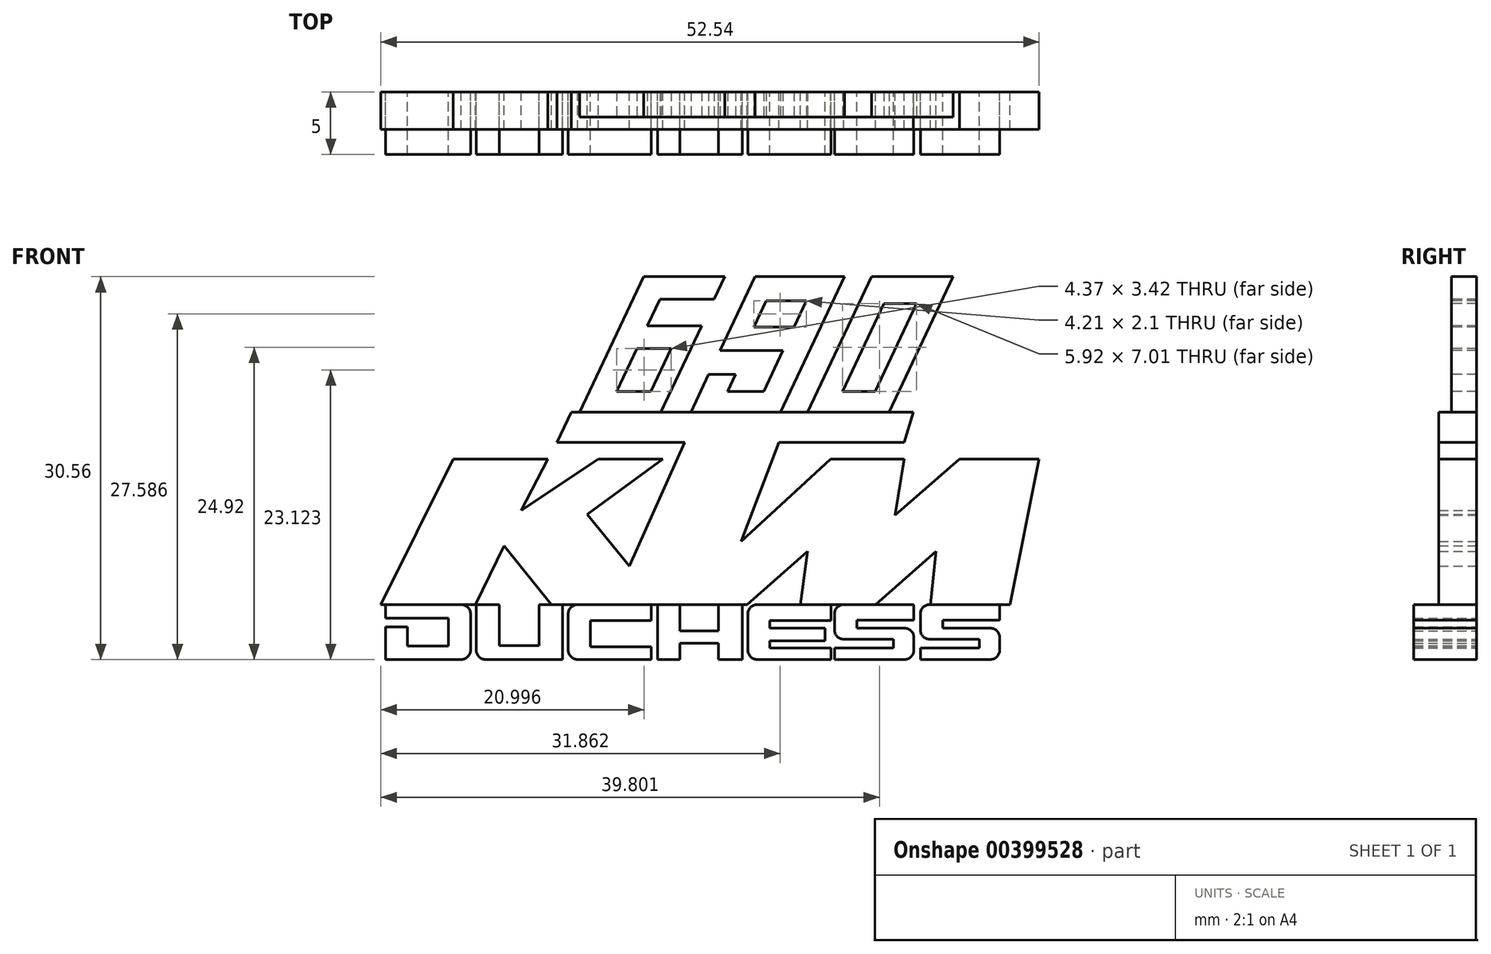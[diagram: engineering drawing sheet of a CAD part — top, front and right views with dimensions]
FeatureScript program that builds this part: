
annotation { "Feature Type Name" : "Feature", "Feature Type Description" : "" }
export const myFeature = defineFeature(function(context is Context, id is Id, definition is map)
    precondition{}
    {
        {
            var Q0;
            Q0=qCreatedBy(makeId("Front.planeOp"),FACE);
            var sketch = newSketch(context, id + "F0", { "sketchPlane" : qUnion([Q0])});
            skLineSegment(sketch, "E0", {"start": v(-21, 3.08) * mm, "end": v(-26.77, -8.53) * mm});
            skLineSegment(sketch, "E1", {"start": v(-19.24, -8.53) * mm, "end": v(-16.95, -3.85) * mm});
            skLineSegment(sketch, "E2", {"start": v(-16.95, -3.85) * mm, "end": v(-13.14, -8.53) * mm});
            skLineSegment(sketch, "E3", {"start": v(2.46, -8.53) * mm, "end": v(7.3, -4.3) * mm});
            skLineSegment(sketch, "E4", {"start": v(7.3, -4.3) * mm, "end": v(6.73, -8.53) * mm});
            skLineSegment(sketch, "E5", {"start": v(12.72, -8.53) * mm, "end": v(17.55, -4.3) * mm});
            skLineSegment(sketch, "E6", {"start": v(17.55, -4.3) * mm, "end": v(17.09, -8.53) * mm});
            skLineSegment(sketch, "E7", {"start": v(22.64, -8.53) * mm, "end": v(23.45, -8.53) * mm});
            skLineSegment(sketch, "E8", {"start": v(23.45, -8.53) * mm, "end": v(25.77, 3.08) * mm});
            skLineSegment(sketch, "E9", {"start": v(25.77, 3.08) * mm, "end": v(19.43, 3.08) * mm});
            skLineSegment(sketch, "E10", {"start": v(19.43, 3.08) * mm, "end": v(14.26, -1.4) * mm});
            skLineSegment(sketch, "E11", {"start": v(14.26, -1.4) * mm, "end": v(15.01, 3.08) * mm});
            skLineSegment(sketch, "E12", {"start": v(15.01, 3.08) * mm, "end": v(9.11, 3.08) * mm});
            skLineSegment(sketch, "E13", {"start": v(9.11, 3.08) * mm, "end": v(1.98, -3.5) * mm});
            skLineSegment(sketch, "E14", {"start": v(1.98, -3.5) * mm, "end": v(5, 4.43) * mm});
            skLineSegment(sketch, "E15", {"start": v(5, 4.43) * mm, "end": v(15.01, 4.43) * mm});
            skLineSegment(sketch, "E16", {"start": v(15.01, 4.43) * mm, "end": v(15.73, 6.81) * mm});
            skLineSegment(sketch, "E17", {"start": v(-11.58, 6.81) * mm, "end": v(-12.71, 4.43) * mm});
            skLineSegment(sketch, "E18", {"start": v(-12.71, 4.43) * mm, "end": v(-2.53, 4.43) * mm});
            skLineSegment(sketch, "E19", {"start": v(-2.53, 4.43) * mm, "end": v(-6.92, -5.47) * mm});
            skLineSegment(sketch, "E20", {"start": v(-6.92, -5.47) * mm, "end": v(-10.29, -1.32) * mm});
            skLineSegment(sketch, "E21", {"start": v(-10.29, -1.32) * mm, "end": v(-4.27, 3.08) * mm});
            skLineSegment(sketch, "E22", {"start": v(-4.27, 3.08) * mm, "end": v(-9.42, 3.08) * mm});
            skLineSegment(sketch, "E23", {"start": v(-9.42, 3.08) * mm, "end": v(-15.58, -1.03) * mm});
            skLineSegment(sketch, "E24", {"start": v(-15.58, -1.03) * mm, "end": v(-13.45, 3.08) * mm});
            skLineSegment(sketch, "E25", {"start": v(-13.45, 3.08) * mm, "end": v(-21, 3.08) * mm});
            skLineSegment(sketch, "E26", {"start": v(-26.4, -8.53) * mm, "end": v(-26.4, -9.64) * mm});
            skLineSegment(sketch, "E27", {"start": v(-26.4, -12.92) * mm, "end": v(-20.36, -12.92) * mm});
            skLineSegment(sketch, "E28", {"start": v(-19.6, -12.17) * mm, "end": v(-19.6, -9.28) * mm});
            skPoint(sketch, "E29.visualSharp", {"position": v(-19.6, -8.53) * mm});
            skArc(sketch, "E29.filletArc", {"start": v(-19.6, -9.28) * mm, "mid": v(-19.83, -8.75) * mm, "end": v(-20.36, -8.53) * mm});
            skPoint(sketch, "E30.visualSharp", {"position": v(-19.6, -12.92) * mm});
            skArc(sketch, "E30.filletArc", {"start": v(-20.36, -12.92) * mm, "mid": v(-19.83, -12.7) * mm, "end": v(-19.6, -12.17) * mm});
            skLineSegment(sketch, "E31", {"start": v(-24.66, -10.31) * mm, "end": v(-24.66, -11.84) * mm});
            skLineSegment(sketch, "E32", {"start": v(-24.66, -11.84) * mm, "end": v(-21.39, -11.84) * mm});
            skLineSegment(sketch, "E33", {"start": v(-21.39, -11.84) * mm, "end": v(-21.39, -9.64) * mm});
            skLineSegment(sketch, "E34", {"start": v(-21.39, -9.64) * mm, "end": v(-26.4, -9.64) * mm});
            skLineSegment(sketch, "E35", {"start": v(-24.66, -10.31) * mm, "end": v(-26.4, -10.31) * mm});
            skLineSegment(sketch, "E36.trimOffspring", {"start": v(-26.4, -10.31) * mm, "end": v(-26.4, -12.92) * mm});
            skLineSegment(sketch, "E37", {"start": v(-20.36, -8.53) * mm, "end": v(-19.17, -8.53) * mm, "construction": true});
            skLineSegment(sketch, "E38", {"start": v(-19.17, -8.53) * mm, "end": v(-19.17, -12.17) * mm});
            skLineSegment(sketch, "E39", {"start": v(-17.3, -8.53) * mm, "end": v(-17.3, -11.81) * mm});
            skLineSegment(sketch, "E40", {"start": v(-17.3, -11.81) * mm, "end": v(-14.13, -11.81) * mm});
            skLineSegment(sketch, "E41", {"start": v(-14.13, -11.81) * mm, "end": v(-14.13, -8.53) * mm});
            skLineSegment(sketch, "E42", {"start": v(-14.13, -8.53) * mm, "end": v(-13.14, -8.53) * mm});
            skLineSegment(sketch, "E43", {"start": v(-12.28, -8.53) * mm, "end": v(-12.28, -12.92) * mm});
            skLineSegment(sketch, "E44", {"start": v(-12.28, -12.92) * mm, "end": v(-18.42, -12.92) * mm});
            skPoint(sketch, "E45.visualSharp", {"position": v(-19.17, -12.92) * mm});
            skArc(sketch, "E45.filletArc", {"start": v(-19.17, -12.17) * mm, "mid": v(-18.95, -12.7) * mm, "end": v(-18.42, -12.92) * mm});
            skLineSegment(sketch, "E46", {"start": v(-19.17, -8.53) * mm, "end": v(-17.3, -8.53) * mm});
            skLineSegment(sketch, "E47", {"start": v(-11.82, -9.28) * mm, "end": v(-11.82, -12.17) * mm});
            skLineSegment(sketch, "E48", {"start": v(-5.18, -8.53) * mm, "end": v(-5.18, -9.8) * mm});
            skLineSegment(sketch, "E49", {"start": v(-5.18, -9.8) * mm, "end": v(-10.05, -9.8) * mm});
            skLineSegment(sketch, "E50", {"start": v(-10.05, -9.8) * mm, "end": v(-10.05, -11.91) * mm});
            skLineSegment(sketch, "E51", {"start": v(-10.05, -11.91) * mm, "end": v(-5.18, -11.91) * mm});
            skLineSegment(sketch, "E52", {"start": v(-5.18, -11.91) * mm, "end": v(-5.18, -12.92) * mm});
            skLineSegment(sketch, "E53", {"start": v(-11.07, -12.92) * mm, "end": v(-5.18, -12.92) * mm});
            skPoint(sketch, "E54.visualSharp", {"position": v(-11.82, -12.92) * mm});
            skArc(sketch, "E54.filletArc", {"start": v(-11.82, -12.17) * mm, "mid": v(-11.6, -12.7) * mm, "end": v(-11.07, -12.92) * mm});
            skPoint(sketch, "E55.visualSharp", {"position": v(-11.82, -8.53) * mm});
            skArc(sketch, "E55.filletArc", {"start": v(-11.07, -8.53) * mm, "mid": v(-11.6, -8.75) * mm, "end": v(-11.82, -9.28) * mm});
            skLineSegment(sketch, "E56", {"start": v(-4.69, -8.53) * mm, "end": v(-4.69, -12.92) * mm});
            skLineSegment(sketch, "E57", {"start": v(-4.69, -12.92) * mm, "end": v(-2.9, -12.92) * mm});
            skLineSegment(sketch, "E58", {"start": v(-2.9, -12.92) * mm, "end": v(-2.9, -11.62) * mm});
            skLineSegment(sketch, "E59", {"start": v(-2.9, -11.62) * mm, "end": v(0.17, -11.62) * mm});
            skLineSegment(sketch, "E60", {"start": v(0.17, -11.62) * mm, "end": v(0.17, -12.92) * mm});
            skLineSegment(sketch, "E61", {"start": v(0.17, -12.92) * mm, "end": v(2.1, -12.92) * mm});
            skLineSegment(sketch, "E62", {"start": v(2.1, -12.92) * mm, "end": v(2.1, -8.53) * mm});
            skLineSegment(sketch, "E63", {"start": v(0.17, -8.53) * mm, "end": v(0.17, -10.63) * mm});
            skLineSegment(sketch, "E64", {"start": v(0.17, -10.63) * mm, "end": v(-2.9, -10.63) * mm});
            skLineSegment(sketch, "E65", {"start": v(-2.9, -10.63) * mm, "end": v(-2.9, -8.53) * mm});
            skLineSegment(sketch, "E66", {"start": v(2.52, -9.28) * mm, "end": v(2.52, -12.17) * mm});
            skLineSegment(sketch, "E67", {"start": v(9.16, -8.53) * mm, "end": v(9.16, -9.8) * mm});
            skLineSegment(sketch, "E68", {"start": v(9.16, -9.8) * mm, "end": v(4.28, -9.8) * mm});
            skLineSegment(sketch, "E69", {"start": v(4.28, -9.8) * mm, "end": v(4.28, -10.41) * mm});
            skLineSegment(sketch, "E70", {"start": v(4.28, -12) * mm, "end": v(9.16, -12) * mm});
            skLineSegment(sketch, "E71", {"start": v(9.16, -12) * mm, "end": v(9.16, -12.92) * mm});
            skLineSegment(sketch, "E72", {"start": v(3.27, -12.92) * mm, "end": v(9.16, -12.92) * mm});
            skPoint(sketch, "E73.visualSharp", {"position": v(2.52, -12.92) * mm});
            skArc(sketch, "E73.filletArc", {"start": v(2.52, -12.17) * mm, "mid": v(2.74, -12.7) * mm, "end": v(3.27, -12.92) * mm});
            skLineSegment(sketch, "E74", {"start": v(3.27, -8.53) * mm, "end": v(6.73, -8.53) * mm});
            skPoint(sketch, "E75.visualSharp", {"position": v(2.52, -8.53) * mm});
            skArc(sketch, "E75.filletArc", {"start": v(3.27, -8.53) * mm, "mid": v(2.74, -8.75) * mm, "end": v(2.52, -9.28) * mm});
            skLineSegment(sketch, "E76", {"start": v(8.69, -10.41) * mm, "end": v(4.28, -10.41) * mm});
            skLineSegment(sketch, "E77", {"start": v(8.69, -10.41) * mm, "end": v(8.69, -11.45) * mm});
            skLineSegment(sketch, "E78", {"start": v(8.69, -11.45) * mm, "end": v(4.28, -11.45) * mm});
            skLineSegment(sketch, "E79.trimOffspring", {"start": v(4.28, -11.45) * mm, "end": v(4.28, -12) * mm});
            skLineSegment(sketch, "E80", {"start": v(15.78, -8.53) * mm, "end": v(15.78, -9.77) * mm});
            skLineSegment(sketch, "E81", {"start": v(15.78, -9.77) * mm, "end": v(11.21, -9.77) * mm});
            skLineSegment(sketch, "E82", {"start": v(11.21, -9.77) * mm, "end": v(11.21, -10.42) * mm});
            skLineSegment(sketch, "E83", {"start": v(11.21, -10.42) * mm, "end": v(15.03, -10.42) * mm});
            skLineSegment(sketch, "E84", {"start": v(15.78, -11.17) * mm, "end": v(15.78, -12.17) * mm});
            skLineSegment(sketch, "E85", {"start": v(15.03, -12.92) * mm, "end": v(9.43, -12.92) * mm});
            skLineSegment(sketch, "E86", {"start": v(9.43, -12.92) * mm, "end": v(9.43, -12) * mm});
            skLineSegment(sketch, "E87", {"start": v(9.43, -12) * mm, "end": v(14.16, -12) * mm});
            skLineSegment(sketch, "E88", {"start": v(14.16, -12) * mm, "end": v(14.16, -11.3) * mm});
            skLineSegment(sketch, "E89", {"start": v(14.16, -11.3) * mm, "end": v(10.18, -11.3) * mm});
            skLineSegment(sketch, "E90", {"start": v(9.43, -10.55) * mm, "end": v(9.43, -9.28) * mm});
            skLineSegment(sketch, "E91", {"start": v(12.72, -8.53) * mm, "end": v(15.78, -8.53) * mm});
            skPoint(sketch, "E92.visualSharp", {"position": v(9.43, -8.53) * mm});
            skArc(sketch, "E92.filletArc", {"start": v(10.18, -8.53) * mm, "mid": v(9.65, -8.75) * mm, "end": v(9.43, -9.28) * mm});
            skPoint(sketch, "E93.visualSharp", {"position": v(9.43, -11.3) * mm});
            skArc(sketch, "E93.filletArc", {"start": v(9.43, -10.55) * mm, "mid": v(9.65, -11.08) * mm, "end": v(10.18, -11.3) * mm});
            skPoint(sketch, "E94.visualSharp", {"position": v(15.78, -10.42) * mm});
            skArc(sketch, "E94.filletArc", {"start": v(15.78, -11.17) * mm, "mid": v(15.56, -10.64) * mm, "end": v(15.03, -10.42) * mm});
            skPoint(sketch, "E95.visualSharp", {"position": v(15.78, -12.92) * mm});
            skArc(sketch, "E95.filletArc", {"start": v(15.03, -12.92) * mm, "mid": v(15.56, -12.7) * mm, "end": v(15.78, -12.17) * mm});
            skLineSegment(sketch, "E96", {"start": v(22.64, -8.53) * mm, "end": v(22.64, -9.77) * mm});
            skLineSegment(sketch, "E97", {"start": v(22.64, -9.77) * mm, "end": v(18.07, -9.77) * mm});
            skLineSegment(sketch, "E98", {"start": v(18.07, -9.77) * mm, "end": v(18.07, -10.42) * mm});
            skLineSegment(sketch, "E99", {"start": v(18.07, -10.42) * mm, "end": v(21.89, -10.42) * mm});
            skLineSegment(sketch, "E100", {"start": v(22.64, -11.17) * mm, "end": v(22.64, -12.17) * mm});
            skLineSegment(sketch, "E101", {"start": v(21.89, -12.92) * mm, "end": v(16.29, -12.92) * mm});
            skLineSegment(sketch, "E102", {"start": v(16.29, -12.92) * mm, "end": v(16.29, -12) * mm});
            skLineSegment(sketch, "E103", {"start": v(16.29, -12) * mm, "end": v(21.02, -12) * mm});
            skLineSegment(sketch, "E104", {"start": v(21.02, -12) * mm, "end": v(21.02, -11.3) * mm});
            skLineSegment(sketch, "E105", {"start": v(21.02, -11.3) * mm, "end": v(17.04, -11.3) * mm});
            skLineSegment(sketch, "E106", {"start": v(16.29, -10.55) * mm, "end": v(16.29, -9.28) * mm});
            skLineSegment(sketch, "E107", {"start": v(17.04, -8.53) * mm, "end": v(17.09, -8.53) * mm});
            skPoint(sketch, "E108.visualSharp", {"position": v(16.29, -8.53) * mm});
            skArc(sketch, "E108.filletArc", {"start": v(17.04, -8.53) * mm, "mid": v(16.5, -8.75) * mm, "end": v(16.29, -9.28) * mm});
            skPoint(sketch, "E109.visualSharp", {"position": v(16.29, -11.3) * mm});
            skArc(sketch, "E109.filletArc", {"start": v(16.29, -10.55) * mm, "mid": v(16.5, -11.08) * mm, "end": v(17.04, -11.3) * mm});
            skPoint(sketch, "E110.visualSharp", {"position": v(22.64, -10.42) * mm});
            skArc(sketch, "E110.filletArc", {"start": v(22.64, -11.17) * mm, "mid": v(22.42, -10.64) * mm, "end": v(21.89, -10.42) * mm});
            skPoint(sketch, "E111.visualSharp", {"position": v(22.64, -12.92) * mm});
            skArc(sketch, "E111.filletArc", {"start": v(21.89, -12.92) * mm, "mid": v(22.42, -12.7) * mm, "end": v(22.64, -12.17) * mm});
            skLineSegment(sketch, "E112", {"start": v(23.45, -8.53) * mm, "end": v(22.64, -8.53) * mm});
            skPoint(sketch, "E113.orphan", {"position": v(-13.45, -8.15) * mm});
            skPoint(sketch, "E114.orphan", {"position": v(-19.05, -8.15) * mm});
            skLineSegment(sketch, "E115.trimOffspring", {"start": v(10.18, -8.53) * mm, "end": v(9.16, -8.53) * mm});
            skLineSegment(sketch, "E116.trimOffspring", {"start": v(2.46, -8.53) * mm, "end": v(2.1, -8.53) * mm});
            skLineSegment(sketch, "E117.trimOffspring", {"start": v(-19.24, -8.53) * mm, "end": v(-20.36, -8.53) * mm});
            skLineSegment(sketch, "E118.trimOffspring", {"start": v(-4.69, -8.53) * mm, "end": v(-5.18, -8.53) * mm});
            skLineSegment(sketch, "E119.trimOffspring", {"start": v(-11.07, -8.53) * mm, "end": v(-12.28, -8.53) * mm});
            skLineSegment(sketch, "E120.trimOffspring", {"start": v(-26.4, -8.53) * mm, "end": v(-26.77, -8.53) * mm});
            skLineSegment(sketch, "E121", {"start": v(-2.9, -8.53) * mm, "end": v(0.17, -8.53) * mm});
            skLineSegment(sketch, "E122", {"start": v(-11.58, 6.81) * mm, "end": v(15.73, 6.81) * mm});
            skSolve(sketch);
        }
        {
            var Q0;
            Q0=qSketchRegion(id+"F0",true);
            extrude(context, id + "F1", {"entities" : qUnion([Q0]), "depth" : 5 * mm});
        }
        {
            var Q0;
            Q0=makeQuery(id+"F1.opExtrude","CAP_FACE",FACE,{"disambiguationData":[OSD([sQuery(id+"F0.wireOp",EDGE,"E0"),sQuery(id+"F0.wireOp",EDGE,"E1"),sQuery(id+"F0.wireOp",EDGE,"E2"),sQuery(id+"F0.wireOp",EDGE,"E3"),sQuery(id+"F0.wireOp",EDGE,"E4"),sQuery(id+"F0.wireOp",EDGE,"E5"),sQuery(id+"F0.wireOp",EDGE,"E6"),sQuery(id+"F0.wireOp",EDGE,"E8"),sQuery(id+"F0.wireOp",EDGE,"E9"),sQuery(id+"F0.wireOp",EDGE,"E10"),sQuery(id+"F0.wireOp",EDGE,"E11"),sQuery(id+"F0.wireOp",EDGE,"E12"),sQuery(id+"F0.wireOp",EDGE,"E13"),sQuery(id+"F0.wireOp",EDGE,"E14"),sQuery(id+"F0.wireOp",EDGE,"E15"),sQuery(id+"F0.wireOp",EDGE,"E16"),sQuery(id+"F0.wireOp",EDGE,"3NEIWcZY-8mkg-9U7g-S424-nP58Ebou9Cct"),sQuery(id+"F0.wireOp",EDGE,"E17"),sQuery(id+"F0.wireOp",EDGE,"E18"),sQuery(id+"F0.wireOp",EDGE,"E19"),sQuery(id+"F0.wireOp",EDGE,"E20"),sQuery(id+"F0.wireOp",EDGE,"E21"),sQuery(id+"F0.wireOp",EDGE,"E22"),sQuery(id+"F0.wireOp",EDGE,"E23"),sQuery(id+"F0.wireOp",EDGE,"E24"),sQuery(id+"F0.wireOp",EDGE,"E25"),sQuery(id+"F0.wireOp",EDGE,"E26"),sQuery(id+"F0.wireOp",EDGE,"E27"),sQuery(id+"F0.wireOp",EDGE,"E28"),sQuery(id+"F0.wireOp",EDGE,"E29.filletArc"),sQuery(id+"F0.wireOp",EDGE,"E30.filletArc"),sQuery(id+"F0.wireOp",EDGE,"E31"),sQuery(id+"F0.wireOp",EDGE,"E32"),sQuery(id+"F0.wireOp",EDGE,"E33"),sQuery(id+"F0.wireOp",EDGE,"E34"),sQuery(id+"F0.wireOp",EDGE,"E35"),sQuery(id+"F0.wireOp",EDGE,"E36.trimOffspring"),sQuery(id+"F0.wireOp",EDGE,"E38"),sQuery(id+"F0.wireOp",EDGE,"E39"),sQuery(id+"F0.wireOp",EDGE,"E40"),sQuery(id+"F0.wireOp",EDGE,"E41"),sQuery(id+"F0.wireOp",EDGE,"E42"),sQuery(id+"F0.wireOp",EDGE,"E43"),sQuery(id+"F0.wireOp",EDGE,"E44"),sQuery(id+"F0.wireOp",EDGE,"E45.filletArc"),sQuery(id+"F0.wireOp",EDGE,"E46"),sQuery(id+"F0.wireOp",EDGE,"E47"),sQuery(id+"F0.wireOp",EDGE,"E48"),sQuery(id+"F0.wireOp",EDGE,"E49"),sQuery(id+"F0.wireOp",EDGE,"E50"),sQuery(id+"F0.wireOp",EDGE,"E51"),sQuery(id+"F0.wireOp",EDGE,"E52"),sQuery(id+"F0.wireOp",EDGE,"E53"),sQuery(id+"F0.wireOp",EDGE,"E54.filletArc"),sQuery(id+"F0.wireOp",EDGE,"E55.filletArc"),sQuery(id+"F0.wireOp",EDGE,"E56"),sQuery(id+"F0.wireOp",EDGE,"E57"),sQuery(id+"F0.wireOp",EDGE,"E58"),sQuery(id+"F0.wireOp",EDGE,"E59"),sQuery(id+"F0.wireOp",EDGE,"E60"),sQuery(id+"F0.wireOp",EDGE,"E61"),sQuery(id+"F0.wireOp",EDGE,"E62"),sQuery(id+"F0.wireOp",EDGE,"E63"),sQuery(id+"F0.wireOp",EDGE,"E64"),sQuery(id+"F0.wireOp",EDGE,"E65"),sQuery(id+"F0.wireOp",EDGE,"E66"),sQuery(id+"F0.wireOp",EDGE,"E67"),sQuery(id+"F0.wireOp",EDGE,"E68"),sQuery(id+"F0.wireOp",EDGE,"E69"),sQuery(id+"F0.wireOp",EDGE,"E70"),sQuery(id+"F0.wireOp",EDGE,"E71"),sQuery(id+"F0.wireOp",EDGE,"E72"),sQuery(id+"F0.wireOp",EDGE,"E73.filletArc"),sQuery(id+"F0.wireOp",EDGE,"E74"),sQuery(id+"F0.wireOp",EDGE,"E75.filletArc"),sQuery(id+"F0.wireOp",EDGE,"E76"),sQuery(id+"F0.wireOp",EDGE,"E77"),sQuery(id+"F0.wireOp",EDGE,"E78"),sQuery(id+"F0.wireOp",EDGE,"E79.trimOffspring"),sQuery(id+"F0.wireOp",EDGE,"E80"),sQuery(id+"F0.wireOp",EDGE,"E81"),sQuery(id+"F0.wireOp",EDGE,"E82"),sQuery(id+"F0.wireOp",EDGE,"E83"),sQuery(id+"F0.wireOp",EDGE,"E84"),sQuery(id+"F0.wireOp",EDGE,"E85"),sQuery(id+"F0.wireOp",EDGE,"E86"),sQuery(id+"F0.wireOp",EDGE,"E87"),sQuery(id+"F0.wireOp",EDGE,"E88"),sQuery(id+"F0.wireOp",EDGE,"E89"),sQuery(id+"F0.wireOp",EDGE,"E90"),sQuery(id+"F0.wireOp",EDGE,"E91"),sQuery(id+"F0.wireOp",EDGE,"E92.filletArc"),sQuery(id+"F0.wireOp",EDGE,"E93.filletArc"),sQuery(id+"F0.wireOp",EDGE,"E94.filletArc"),sQuery(id+"F0.wireOp",EDGE,"E95.filletArc"),sQuery(id+"F0.wireOp",EDGE,"E96"),sQuery(id+"F0.wireOp",EDGE,"E97"),sQuery(id+"F0.wireOp",EDGE,"E98"),sQuery(id+"F0.wireOp",EDGE,"E99"),sQuery(id+"F0.wireOp",EDGE,"E100"),sQuery(id+"F0.wireOp",EDGE,"E101"),sQuery(id+"F0.wireOp",EDGE,"E102"),sQuery(id+"F0.wireOp",EDGE,"E103"),sQuery(id+"F0.wireOp",EDGE,"E104"),sQuery(id+"F0.wireOp",EDGE,"E105"),sQuery(id+"F0.wireOp",EDGE,"E106"),sQuery(id+"F0.wireOp",EDGE,"E107"),sQuery(id+"F0.wireOp",EDGE,"E108.filletArc"),sQuery(id+"F0.wireOp",EDGE,"E109.filletArc"),sQuery(id+"F0.wireOp",EDGE,"E110.filletArc"),sQuery(id+"F0.wireOp",EDGE,"E111.filletArc"),sQuery(id+"F0.wireOp",EDGE,"E112"),sQuery(id+"F0.wireOp",EDGE,"E115.trimOffspring"),sQuery(id+"F0.wireOp",EDGE,"E116.trimOffspring"),sQuery(id+"F0.wireOp",EDGE,"E117.trimOffspring"),sQuery(id+"F0.wireOp",EDGE,"E118.trimOffspring"),sQuery(id+"F0.wireOp",EDGE,"E119.trimOffspring"),sQuery(id+"F0.wireOp",EDGE,"E120.trimOffspring"),sQuery(id+"F0.wireOp",EDGE,"E121")])],"isStart":false});
            var sketch = newSketch(context, id + "F2", { "sketchPlane" : qUnion([Q0])});
            skLineSegment(sketch, "E123.bottom", {"start": v(-26.77, -8.53) * mm, "end": v(26.52, -8.53) * mm});
            skLineSegment(sketch, "E123.top", {"start": v(-26.77, 6.81) * mm, "end": v(2.1, 6.81) * mm});
            skLineSegment(sketch, "E123.left", {"start": v(-26.77, -8.53) * mm, "end": v(-26.77, 6.81) * mm});
            skLineSegment(sketch, "E123.right", {"start": v(26.52, -8.53) * mm, "end": v(26.52, 6.81) * mm});
            skLineSegment(sketch, "E124", {"start": v(-10.91, 6.81) * mm, "end": v(-5.8, 17.64) * mm});
            skLineSegment(sketch, "E125", {"start": v(-5.8, 17.64) * mm, "end": v(0.69, 17.64) * mm});
            skLineSegment(sketch, "E126", {"start": v(-0.17, 15.83) * mm, "end": v(-4.5, 15.83) * mm});
            skLineSegment(sketch, "E127", {"start": v(-4.5, 15.83) * mm, "end": v(-5.5, 13.71) * mm});
            skLineSegment(sketch, "E128", {"start": v(-5.5, 13.71) * mm, "end": v(-1.17, 13.71) * mm});
            skLineSegment(sketch, "E129", {"start": v(0.69, 17.64) * mm, "end": v(-0.17, 15.83) * mm});
            skLineSegment(sketch, "E130.0", {"start": v(-6.34, 11.91) * mm, "end": v(-3.6, 11.91) * mm});
            skLineSegment(sketch, "E131", {"start": v(-6.34, 11.91) * mm, "end": v(-7.96, 8.5) * mm});
            skLineSegment(sketch, "E132", {"start": v(-7.96, 8.5) * mm, "end": v(-5.2, 8.5) * mm});
            skLineSegment(sketch, "E133", {"start": v(-5.2, 8.5) * mm, "end": v(-3.6, 11.91) * mm});
            skLineSegment(sketch, "E134", {"start": v(3.09, 17.64) * mm, "end": v(10.23, 17.64) * mm});
            skLineSegment(sketch, "E135", {"start": v(10.23, 17.64) * mm, "end": v(5.12, 6.81) * mm});
            skLineSegment(sketch, "E136", {"start": v(3.78, 8.5) * mm, "end": v(5.32, 11.74) * mm});
            skLineSegment(sketch, "E137", {"start": v(5.32, 11.74) * mm, "end": v(0.3, 11.74) * mm});
            skLineSegment(sketch, "E138", {"start": v(3.09, 17.64) * mm, "end": v(0.3, 11.74) * mm});
            skLineSegment(sketch, "E139.trimOffspring", {"start": v(-1.17, 13.71) * mm, "end": v(-4.43, 6.81) * mm});
            skPoint(sketch, "E140.orphan", {"position": v(1.1, 17.64) * mm});
            skLineSegment(sketch, "E141.trimOffspring", {"start": v(4.23, 6.81) * mm, "end": v(26.52, 6.81) * mm});
            skLineSegment(sketch, "E142", {"start": v(2.1, 6.81) * mm, "end": v(4.23, 6.81) * mm});
            skLineSegment(sketch, "E143", {"start": v(-0.6, 9.83) * mm, "end": v(-2.03, 6.81) * mm});
            skLineSegment(sketch, "E144", {"start": v(-0.6, 9.83) * mm, "end": v(1.55, 9.83) * mm});
            skPoint(sketch, "E144.startSnap0", {"position": v(-4.97, 11.91) * mm});
            skLineSegment(sketch, "E145", {"start": v(1.55, 9.83) * mm, "end": v(0.92, 8.5) * mm});
            skLineSegment(sketch, "E146.trimOffspring", {"start": v(0.92, 8.5) * mm, "end": v(3.78, 8.5) * mm});
            skLineSegment(sketch, "E147", {"start": v(3.98, 15.72) * mm, "end": v(2.99, 13.62) * mm});
            skLineSegment(sketch, "E148", {"start": v(2.99, 13.62) * mm, "end": v(6.2, 13.62) * mm});
            skLineSegment(sketch, "E149", {"start": v(3.98, 15.72) * mm, "end": v(7.2, 15.72) * mm});
            skLineSegment(sketch, "E150", {"start": v(6.2, 13.62) * mm, "end": v(7.2, 15.72) * mm});
            skLineSegment(sketch, "E151", {"start": v(7.3, 6.81) * mm, "end": v(12.42, 17.64) * mm});
            skLineSegment(sketch, "E152", {"start": v(12.42, 17.64) * mm, "end": v(18.9, 17.64) * mm});
            skLineSegment(sketch, "E153.0", {"start": v(13.38, 15.5) * mm, "end": v(16, 15.5) * mm});
            skLineSegment(sketch, "E154", {"start": v(13.38, 15.5) * mm, "end": v(10.07, 8.5) * mm});
            skLineSegment(sketch, "E155", {"start": v(10.07, 8.5) * mm, "end": v(12.68, 8.5) * mm});
            skLineSegment(sketch, "E156", {"start": v(12.68, 8.5) * mm, "end": v(16, 15.5) * mm});
            skLineSegment(sketch, "E157.trimOffspring", {"start": v(18.9, 17.64) * mm, "end": v(13.79, 6.81) * mm});
            skSolve(sketch);
        }
        {
            var Q0;
            Q0=qSketchRegion(id+"F2",true);
            extrude(context, id + "F3", {"entities" : qUnion([Q0]), "operationType" : NewBodyOperationType.REMOVE, "oppositeDirection" : true, "depth" : 2 * mm});
        }
        {
            var Q0;
            {var subQ0=sQuery(id+"F2.wireOp",EDGE,"E124");Q0=makeQuery(id+"F2.imprint","IMPRINT",FACE,{"disambiguationData":[TD([[makeQuery(id+"F2.imprint","IMPRINT",EDGE,{"derivedFrom":subQ0}),-1.0]])]});}
            var Q1;
            Q1=makeQuery(id+"F2.imprint","IMPRINT",FACE,{"disambiguationData":[TD([[makeQuery(id+"F2.imprint","IMPRINT",EDGE,{"derivedFrom":sQuery(id+"F2.wireOp",EDGE,"E134")}),-1.0]])]});
            var Q2;
            {var subQ0=sQuery(id+"F2.wireOp",EDGE,"E151");Q2=makeQuery(id+"F2.imprint","IMPRINT",FACE,{"disambiguationData":[TD([[makeQuery(id+"F2.imprint","IMPRINT",EDGE,{"derivedFrom":subQ0}),-1.0]])]});}
            extrude(context, id + "F4", {"entities" : qUnion([Q0, Q1, Q2]), "operationType" : NewBodyOperationType.ADD, "oppositeDirection" : true, "depth" : 5 * mm, "hasSecondDirection" : true, "secondDirectionOppositeDirection" : true, "secondDirectionDepth" : 3 * mm});
        }
    });
